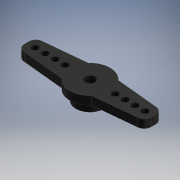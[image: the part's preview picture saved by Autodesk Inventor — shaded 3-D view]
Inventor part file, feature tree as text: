
AUTODESK INVENTOR PART (.ipt)
format: ipt  version: 2018.3 (Build 223284000, 284)  size: 168,960 bytes
history: native  units: mm
features: chamfer x4, extrude x3, sketch x3, fillet x1
ambient origin geometry x8: Origin, YZ Plane, XZ Plane, XY Plane, X Axis, Y Axis, Z Axis, Center Point
bodies: Solid1 (feature_tree)
feature tree (11):
  extrude  "Extrusion1"  Depth=3.0mm
  fillet  "Fillet1"  Radius=17.5mm
  chamfer  "Chamfer6"  Distance=2.5mm
  chamfer  "Chamfer7"  Distance=1.5mm Angle=45.0deg
  chamfer  "Chamfer8"  Distance=1.5mm Angle=45.0deg
  chamfer  "Chamfer9"  Distance=1.5mm Angle=45.0deg
  extrude  "Extrusion3"  Depth=1.5mm TaperAngle=45.0deg
  extrude  "Extrusion4"  Depth=2.0mm
  sketch  "Sketch1"  dims[d0=3.0mm d1=12.0mm d2=17.5mm]
  sketch  "Sketch3"  dims[d3=5.5mm d4=2.5mm d5=0.0mm]
  sketch  "Sketch4"  dims[d18=2.0mm d22=11.6666mm d23=1.5mm d24=45.0deg d25=11.6666mm d26=1.5mm d27=45.0deg d28=11.6666mm d29=1.5mm d30=45.0deg d31=11.6666mm d32=1.5mm d33=45.0deg d37=2.0mm d38=7.5mm d39=40.0mm d41=3.0mm d42=10.0mm d44=10.0mm d46=2.0mm d47=0.0mm d48=5.0mm d49=8.5mm d50=3.0mm d51=0.0mm]
